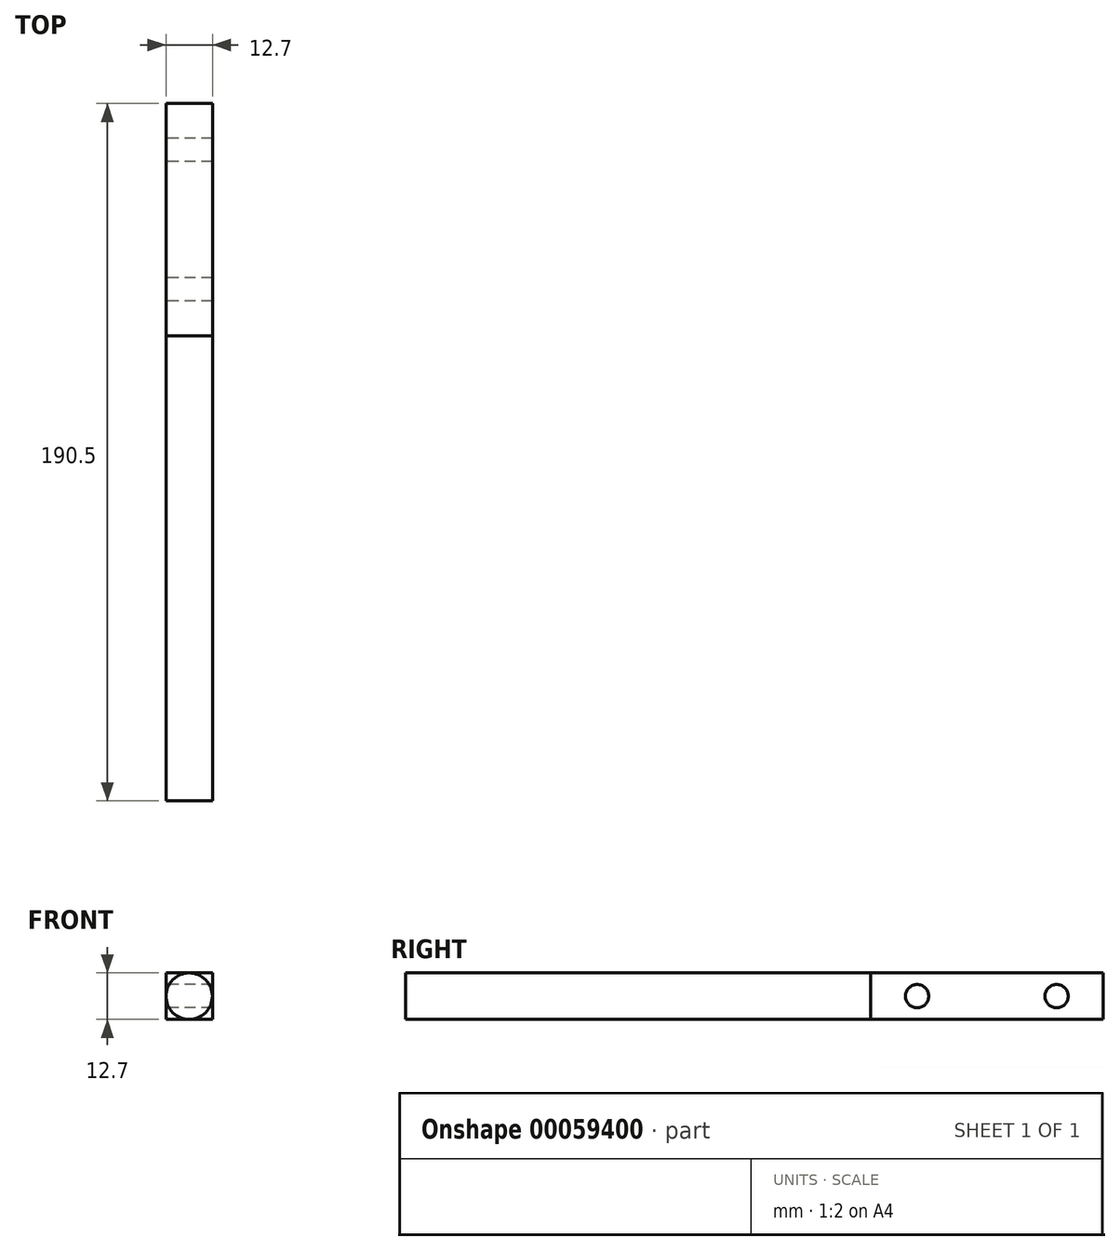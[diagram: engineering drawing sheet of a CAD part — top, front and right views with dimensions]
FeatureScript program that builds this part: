
annotation { "Feature Type Name" : "Feature", "Feature Type Description" : "" }
export const myFeature = defineFeature(function(context is Context, id is Id, definition is map)
    precondition{}
    {
        {
            var Q0;
            Q0=qCreatedBy(makeId("Front.planeOp"),FACE);
            var sketch = newSketch(context, id + "F0", { "sketchPlane" : qUnion([Q0])});
            skLineSegment(sketch, "E0.bottom", {"start": v(0, 0) * mm, "end": v(12.7, 0) * mm});
            skLineSegment(sketch, "E0.top", {"start": v(0, -12.7) * mm, "end": v(12.7, -12.7) * mm});
            skLineSegment(sketch, "E0.left", {"start": v(0, 0) * mm, "end": v(0, -12.7) * mm});
            skLineSegment(sketch, "E0.right", {"start": v(12.7, 0) * mm, "end": v(12.7, -12.7) * mm});
            skSolve(sketch);
        }
        {
            var Q0;
            Q0 = qSketchRegion(id + "F0", true);
            extrude(context, id + "F1", {"entities" : qUnion([Q0]), "oppositeDirection" : true, "depth" : 63.5 * mm});
        }
        {
            var Q0;
            Q0=makeQuery(id+"F1.opExtrude","CAP_FACE",FACE,{"disambiguationData":[OSD([sQuery(id+"F0.wireOp",EDGE,"E0.bottom"),sQuery(id+"F0.wireOp",EDGE,"E0.top"),sQuery(id+"F0.wireOp",EDGE,"E0.left"),sQuery(id+"F0.wireOp",EDGE,"E0.right")])],"isStart":true});
            var sketch = newSketch(context, id + "F2", { "sketchPlane" : qUnion([Q0])});
            skCircle(sketch, "E1", {"center": v(6.35, -6.35) * mm, "radius": 6.35 * mm});
            skLineSegment(sketch, "E2", {"start": v(6.35, -16.8) * mm, "end": v(6.35, 4.1) * mm, "construction": true});
            skPoint(sketch, "E2.startSnap0", {"position": v(6.35, -12.7) * mm});
            skPoint(sketch, "E2.endSnap0", {"position": v(6.35, 0) * mm});
            skLineSegment(sketch, "E3", {"start": v(17.26, -6.35) * mm, "end": v(-3.74, -6.35) * mm, "construction": true});
            skPoint(sketch, "E3.startSnap0", {"position": v(12.7, -6.35) * mm});
            skSolve(sketch);
        }
        {
            var Q0;
            Q0 = qSketchRegion(id + "F2", true);
            extrude(context, id + "F3", {"entities" : qUnion([Q0]), "operationType" : NewBodyOperationType.ADD, "depth" : 127 * mm});
        }
        {
            var Q0;
            Q0=makeQuery(id+"F1.opExtrude","SWEPT_FACE",FACE,{"disambiguationData":[OSD([sQuery(id+"F0.wireOp",EDGE,"E0.left")])]});
            var sketch = newSketch(context, id + "F4", { "sketchPlane" : qUnion([Q0])});
            skLineSegment(sketch, "E4", {"start": v(-70.25, -6.35) * mm, "end": v(10.78, -6.35) * mm, "construction": true});
            skPoint(sketch, "E4.startSnap0", {"position": v(-63.5, -6.35) * mm});
            skCircle(sketch, "E5", {"center": v(-50.8, -6.35) * mm, "radius": 3.18 * mm});
            skCircle(sketch, "E6", {"center": v(-12.7, -6.35) * mm, "radius": 3.18 * mm});
            skSolve(sketch);
        }
        {
            var Q0;
            Q0 = qSketchRegion(id + "F4", true);
            extrude(context, id + "F5", {"entities" : qUnion([Q0]), "operationType" : NewBodyOperationType.REMOVE, "oppositeDirection" : true, "depth" : 25.4 * mm});
        }
    });
